SOLIDWORKS PART (.sldprt)
format: sldprt  version: not decoded by parser v0  size: 20,868,096 bytes
history: native  units: mm
features: sketch x42, extrude x29, chamfer x18, pattern_linear x9, cut_extrude x7, fillet x6, plane x3, hole x2, material x1, revolve x1, mirror x1 (+13 scaffold rows collapsed)
feature tree (132):
  scaffold x13  (default folders/planes/origin — collapsed)
  material  "Material <not specified>"
  sketch  "Sketch1"  dims[D1=58.4708mm D2=76.2mm]
  extrude  "Extrude1"  Depth=1.6256mm
  hole  "1/8 (0.125) Diameter Hole1"  Diameter=3.175mm Depth=1.6256mm
  sketch  "Sketch3"  dims[D1=68.58mm D2=50.8mm]
  sketch  "Sketch2"  dims[hole-wizard template sketch: 60 standard entries collapsed; hole parameters kept: c18.Thru Hole Depth=1.6256mm]
  sketch  "Sketch4"  dims[D1=0.8636mm D2=0.8636mm D3=15.24mm D4=3.81mm D5=12.7mm D6=12.7mm D7=12.7mm]
  extrude  "Extrude2"  Depth=8.89mm
  chamfer  "Chamfer1"  Distance=0.508mm
  chamfer  "Chamfer2"  Distance=0.508mm
  pattern_linear  "LPattern2"  Count1=19 Count2=3 Spacing1=2.54mm Spacing2=2.54mm
  sketch  "Sketch5"  dims[D1=~0.79375mm D2=~0.79375mm D3=~0.79375mm D4=~0.79375mm D5=~0.79375mm D6=~0.79375mm]
  extrude  "Extrude3"  Depth=2.54mm
  chamfer  "Chamfer5"  Distance=0.254mm Angle=45deg
  chamfer  "Chamfer6"  Distance=0.254mm Angle=45deg
  chamfer  "Chamfer9"  Distance=0.254mm Angle=45deg
  chamfer  "Chamfer10"  Distance=0.254mm Angle=45deg
  pattern_linear  "LPattern3"  Count1=19 Count2=1 Spacing1=2.54mm Spacing2=2.54mm
  pattern_linear  "LPattern4"  Count1=19 Count2=3 Spacing1=2.54mm Spacing2=2.54mm
  sketch  "Sketch6"  dims[D1=5.08mm D2=4.445mm D3=30.734mm D4=5.842mm D5=13.335mm D6=13.335mm]
  extrude  "Extrude4"  Depth=0.635mm
  sketch  "Sketch7"  dims[D1=12.5476mm D2=2.032mm D3=2.159mm D4=1.778mm D5=1.27mm D6=2.54mm D7=1.397mm D8=11.9888mm]
  extrude  "Extrude5"  Depth=30.7848mm
  fillet  "Fillet1"  Radius=2.159mm
  sketch  "Sketch8"  dims[D1=17.653mm]
  extrude  "Extrude6"  [1 undecoded]
  fillet  "Fillet2"  Radius=1.27mm
  sketch  "Sketch9"  dims[D1=1.778mm]
  extrude  "Extrude7"  Depth=0.5588mm
  sketch  "Sketch10"  dims[c1.D2=~1.297471mm c1.D4=1.778mm c1.D1=7.8994mm c2.D2=16.256mm c2.D3=14.986mm]
  extrude  "Extrude8"  Depth=5.842mm
  fillet  "Fillet3"  Radius=0.508mm
  sketch  "Sketch11"  dims[c1.D1=1.27mm c1.D2=2.54mm c1.D3=10.16mm c1.D4=2.54mm c1.D5=2.54mm c1.D6=2.54mm c1.D7=2.54mm c1.D8=7.62mm c2.D2=2.54mm]
  cut_extrude  "Cut-Extrude1"  Depth=6.35mm
  plane  "Plane1"  Offset=28.575mm
  sketch  "Sketch15"  dims[D1=25.4mm]
  sketch  "Sketch12"  dims[D1=7.112mm D2=9.906mm D3=7.366mm D4=2.54mm D5=19.05mm]
  extrude  "Extrude9"  Depth=35.179mm
  sketch  "Sketch14"  dims[D1=5.207mm]
  extrude  "Extrude10"  Depth=2.032mm
  sketch  "Sketch16"  dims[D1=5.207mm D2=5.207mm]
  extrude  "Extrude11"  Depth=4.7498mm
  fillet  "Fillet4"  Radius=0.254mm
  fillet  "Fillet5"  Radius=0.254mm
  hole  "#4-40 Tapped Hole1"  Diameter=2.2606mm Depth=7.5946mm
  sketch  "Sketch18"
  sketch  "Sketch17"  dims[hole-wizard template sketch: 29 standard entries collapsed; hole parameters kept: c8.Tap Drill Depth=7.5946mm c8.Thread Major Dia.=2.8448mm c8.Thread Depth=5.6896mm c8.D5=~14.816244mm c8.Drill Angle=118.0deg]
  chamfer  "Chamfer7"  Distance=0.508mm Angle=45deg
  chamfer  "Chamfer8"  Distance=0.508mm Angle=45deg
  sketch  "Sketch19"  dims[D1=0.8636mm D2=9.779mm]
  extrude  "Extrude12"  [1 undecoded]
  chamfer  "Chamfer11"  Distance=0.127mm
  sketch  "Sketch20"  dims[D1=~2.42824mm]
  extrude  "Extrude13"  Depth=2.54mm
  chamfer  "Chamfer12"  Distance=0.254mm Angle=45deg
  pattern_linear  "LPattern5"  Count1=2 Count2=3 Spacing1=2.54mm Spacing2=2.54mm
  sketch  "Sketch21"  dims[D1=0.8636mm D2=0.8636mm D3=5.08mm D4=2.54mm]
  extrude  "Extrude14"  [1 undecoded]
  chamfer  "Chamfer13"  Distance=0.127mm
  chamfer  "Chamfer14"  Distance=0.127mm
  sketch  "Sketch22"  dims[D1=~1.21412mm D2=~1.21412mm D3=~2.42824mm D4=~1.21412mm D5=0.8636mm D6=~0.78232mm D7=~0.78232mm D8=~0.78232mm D9=~0.78232mm]
  extrude  "Extrude15"  [1 undecoded]
  chamfer  "Chamfer15"  Distance=0.254mm Angle=45deg
  pattern_linear  "LPattern6"  Count1=6 Count2=1 Spacing1=2.54mm Spacing2=50mm
  sketch  "Sketch23"  dims[D1=6.985mm D2=10.16mm D3=19.8628mm D4=4.064mm]
  extrude  "Extrude16"  Depth=2.2606mm
  sketch  "Sketch24"  dims[D1=1.905mm]
  cut_extrude  "Cut-Extrude2"  Depth=0.762mm
  sketch  "Sketch25"  dims[D1=10.033mm D2=10.16mm D3=1.651mm D4=4.1275mm D5=2.413mm]
  extrude  "Extrude17"  Depth=3.81mm
  sketch  "Sketch26"  dims[D1=8.763mm]
  extrude  "Extrude18"  Depth=1.016mm
  sketch  "Sketch27"  dims[D1=1.524mm D2=2.54mm D3=0.635mm]
  cut_extrude  "Cut-Extrude3"  Depth=3.175mm
  pattern_linear  "LPattern9"  Count1=2 Count2=4 Spacing1=6.223mm Spacing2=2.4384mm
  sketch  "Sketch28"  dims[D1=2.159mm D2=10.922mm D3=3.556mm D4=10.795mm]
  extrude  "Extrude19"  Depth=1.016mm
  sketch  "Sketch29"  dims[c1.D2=1.397mm c1.D1=2.794mm c2.D2=4.953mm]
  extrude  "Extrude20"  Depth=2.54mm
  fillet  "Fillet6"  Radius=0.254mm
  sketch  "Sketch30"  dims[D1=3.175mm D2=5.842mm D3=0.508mm]
  extrude  "Extrude21"  Depth=2.54mm
  sketch  "Sketch31"  dims[c1.D1=4.572mm c1.D2=8.89mm c1.D3=8.001mm c1.D4=3.175mm c1.D5=15.875mm c2.D4=12.065mm c2.D2=0.889mm c2.D3=4.572mm]
  extrude  "Extrude22"  Depth=10.16mm
  sketch  "Sketch32"  dims[D1=6.35mm D2=8.5852mm D3=5.5372mm D4=3.175mm D5=3.175mm D6=3.302mm D7=1.905mm D8=0.762mm]
  extrude  "Extrude23"  Depth=5.5372mm
  sketch  "Sketch33"  dims[D1=0.635mm D2=0.4318mm D3=0.4318mm D4=0.127mm]
  cut_extrude  "Cut-Extrude4"  Depth=1.27mm
  sketch  "Sketch34"  dims[D1=1.5875mm]
  cut_extrude  "Cut-Extrude5"  Depth=1.27mm
  sketch  "Sketch35"  dims[D1=~1.219158mm D2=2.54mm]
  cut_extrude  "Cut-Extrude6"  Depth=0.0254mm
  sketch  "Sketch36"
  cut_extrude  "Cut-Extrude7"  Depth=0.0254mm
  pattern_linear  "LPattern10"  Count1=2 Count2=2 Spacing1=13.716mm Spacing2=13.716mm
  sketch  "Sketch37"  dims[D1=12.954mm D2=1.3208mm]
  extrude  "Extrude24"  [1 undecoded]
  sketch  "Sketch38"  dims[D1=0.8636mm D2=2.667mm D3=2.54mm]
  extrude  "Extrude25"  [1 undecoded]
  sketch  "Sketch39"  dims[D1=~1.21412mm D2=~1.21412mm D3=~1.21412mm D4=~2.42824mm D5=0.8636mm D6=1.6764mm D7=~0.78232mm D8=~0.78232mm]
  extrude  "Extrude26"  [1 undecoded]
  chamfer  "Chamfer16"  Distance=0.254mm Angle=45deg
  chamfer  "Chamfer17"  Distance=0.127mm
  chamfer  "Chamfer18"  Distance=0.127mm
  pattern_linear  "LPattern11"  Count1=2 Count2=1 Spacing1=2.54mm Spacing2=13.716mm
  sketch  "Sketch40"  dims[D1=0.8636mm D2=2.413mm]
  extrude  "Extrude27"  [1 undecoded]
  sketch  "Sketch41"  dims[D1=~2.42824mm D2=~1.21412mm D3=~1.21412mm D4=0.8636mm D5=~0.610657mm]
  extrude  "Extrude28"  [1 undecoded]
  chamfer  "Chamfer19"  Distance=0.127mm
  chamfer  "Chamfer20"  Distance=0.254mm Angle=45deg
  pattern_linear  "LPattern12"  Count1=2 Count2=1 Spacing1=2.54mm Spacing2=13.716mm
  plane  "Plane2"  Offset=2.6035mm
  sketch  "Sketch42"  dims[D1=2.667mm D2=1.27mm]
  revolve  "Revolve1"  Angle=360deg
  plane  "Plane3"  Offset=0mm
  mirror  "Mirror1"
  sketch  "Sketch43"  dims[D1=3.683mm D2=1.905mm D3=7.62mm]
  extrude  "Extrude29"  Depth=2.286mm
decode coverage: 103 of 115 modeling features carry decoded parameters
note: ~ marks probable driven/reference dimensions
note: 9 parameter values undecoded
summary: no parameter record found for 9 features
note: suppression state not decoded; provenance and decode notes live in map.json
